# Revit family: Haworth_HiYa_MotorDriven_Bench_EU_PRELIMINARY
name_source: partatom
category: Furniture
revit_build: Autodesk Revit 2018 (Build: 20170223_1515(x64)
units: mm (PartAtom-declared; Revit-internal decimal feet)

## family parameters
Always vertical = Yes
Cut with Voids When Loaded = No
OmniClass Number = 23.40.70.14.64.21
OmniClass Title = Systems Furniture
Room Calculation Point = No
Shared = No
Work Plane-Based = No

## types (4) — shared parameters
Actual Height = 65 cm
Assembly Code = E2020200
Cable Height = 2 cm
Description = Haworth - HiYa - Motor Driven - Rectangular - Bench
Height = 65 cm
Leg Height = 61.98 cm
Manufacturer = Haworth
Max. Depth = 189.2 cm
Max. Height = 130 cm
Max. Width = 180 cm
Min. Depth = 149.2 cm
Min. Height = 65 cm
Min. Width = 120 cm
Model = HYMB
Revision Number = 0
Size = Verify Final Dim. w/ Haworth
Standard Depths = 149.2, 169.2, 189.2cm
Standard Widths = 120, 140, 160, 180cm
Table Thickness = 3.02 cm
URL = https://www.haworth.com
URL - Product = https://www.haworth.com
Warranty = http://www.haworth.com

## per-type parameters (varying)
| type | Actual Depth | Actual Width | Cable Chain | Cable Length | Cable Outlet Center | Cable Outlet Round | Cable Outlet U | Cable Snake | Cable Tray | Center Cable Tray Bench | Screen Width | Width | with Screen |
| 140w x 149.2d - with Cable Snake | 149.2 cm | 140 cm | No | 100 cm | Yes | Yes | Yes | Yes | Yes | Yes | 143 cm | 140 cm | Yes |
| 120w x 189.2d - without Screen | 189.2 cm | 120 cm | No | 80 cm | Yes | Yes | Yes | No | Yes | Yes | 123 cm | 120 cm | No |
| 180w x 189.2d - w/o Accessories | 189.2 cm | 180 cm | No | 140 cm | No | No | No | No | No | No | 183 cm | 180 cm | No |
| 160w x 169.2d - with Cable Chain | 169.2 cm | 160 cm | Yes | 120 cm | Yes | Yes | Yes | No | No | Yes | 163 cm | 160 cm | Yes |

## geometry (parser evidence)
native form markers: Sweep x38
no freeform markers — native parametric forms only
